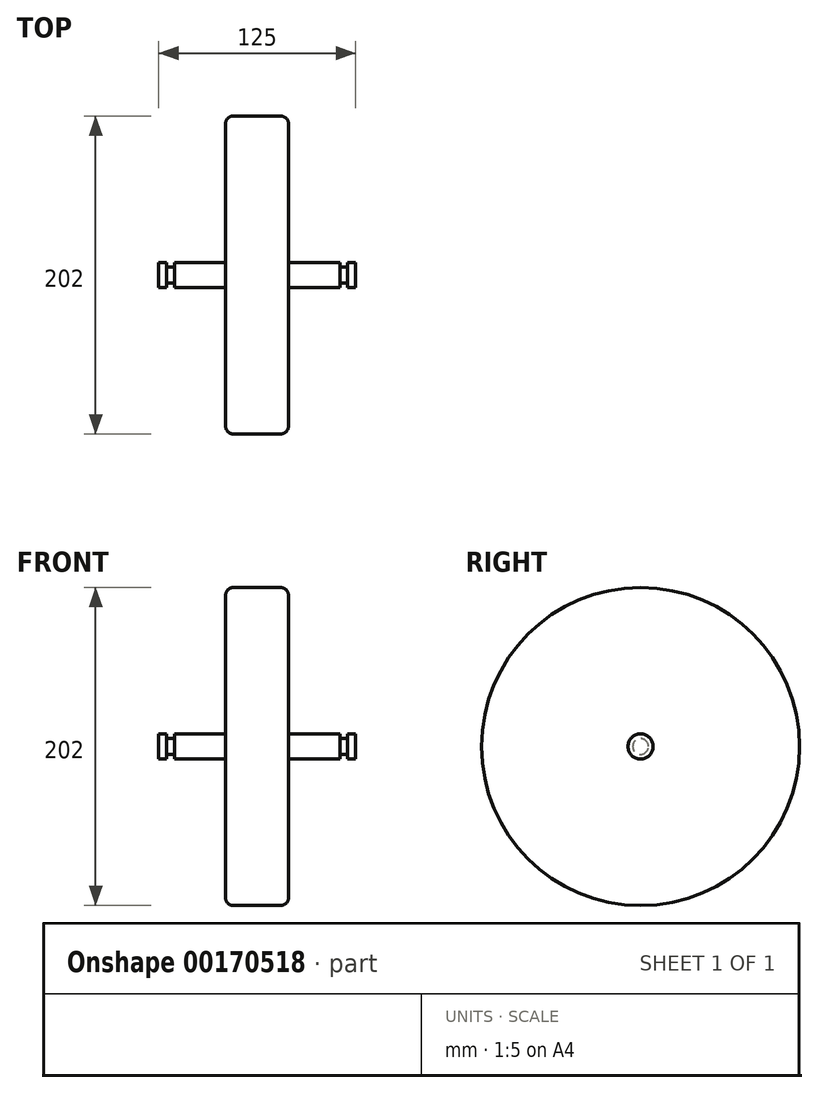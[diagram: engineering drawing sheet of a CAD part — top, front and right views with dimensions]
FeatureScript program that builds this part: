
annotation { "Feature Type Name" : "Feature", "Feature Type Description" : "" }
export const myFeature = defineFeature(function(context is Context, id is Id, definition is map)
    precondition{}
    {
        {
            var Q0;
            Q0=qCreatedBy(makeId("Front.planeOp"),FACE);
            var sketch = newSketch(context, id + "F0", { "sketchPlane" : qUnion([Q0])});
            skLineSegment(sketch, "E0", {"start": v(-87.22, 0) * mm, "end": v(73.7, 0) * mm, "construction": true});
            skLineSegment(sketch, "E1.bottom", {"start": v(-62.5, 8) * mm, "end": v(-57.5, 8) * mm});
            skLineSegment(sketch, "E1.top", {"start": v(-62.5, 0) * mm, "end": v(62.5, 0) * mm});
            skLineSegment(sketch, "E1.left", {"start": v(-62.5, 8) * mm, "end": v(-62.5, 0) * mm});
            skLineSegment(sketch, "E1.right", {"start": v(62.5, 8) * mm, "end": v(62.5, 0) * mm});
            skLineSegment(sketch, "E2.bottom", {"start": v(-15.1, 101) * mm, "end": v(14.9, 101) * mm});
            skLineSegment(sketch, "E2.top", {"start": v(-20.1, 0) * mm, "end": v(19.9, 0) * mm});
            skLineSegment(sketch, "E2.left", {"start": v(-20.1, 96) * mm, "end": v(-20.1, 8) * mm});
            skLineSegment(sketch, "E2.right", {"start": v(19.9, 96) * mm, "end": v(19.9, 8) * mm});
            skLineSegment(sketch, "E3", {"start": v(0, 0) * mm, "end": v(-0.1, 115.13) * mm, "construction": true});
            skPoint(sketch, "E3.endSnap0", {"position": v(-0.1, 101) * mm});
            skPoint(sketch, "E4.visualSharp", {"position": v(-20.1, 101) * mm});
            skArc(sketch, "E4.filletArc", {"start": v(-15.1, 101) * mm, "mid": v(-18.64, 99.54) * mm, "end": v(-20.1, 96) * mm});
            skPoint(sketch, "E5.visualSharp", {"position": v(19.9, 101) * mm});
            skArc(sketch, "E5.filletArc", {"start": v(19.9, 96) * mm, "mid": v(18.43, 99.54) * mm, "end": v(14.9, 101) * mm});
            skLineSegment(sketch, "E6.0", {"start": v(-52.5, 8) * mm, "end": v(-52.5, 5) * mm});
            skLineSegment(sketch, "E7.0", {"start": v(52.5, 8) * mm, "end": v(52.5, 5) * mm});
            skLineSegment(sketch, "E8.0", {"start": v(-57.5, 8) * mm, "end": v(-57.5, 5) * mm});
            skLineSegment(sketch, "E9.0", {"start": v(57.5, 8) * mm, "end": v(57.5, 5) * mm});
            skLineSegment(sketch, "E10.0", {"start": v(-57.5, 5) * mm, "end": v(-52.5, 5) * mm});
            skLineSegment(sketch, "E11.trimOffspring", {"start": v(52.5, 5) * mm, "end": v(57.5, 5) * mm});
            skLineSegment(sketch, "E12.trimOffspring", {"start": v(57.5, 8) * mm, "end": v(62.5, 8) * mm});
            skLineSegment(sketch, "E13.trimOffspring", {"start": v(-52.5, 8) * mm, "end": v(-20.1, 8) * mm});
            skLineSegment(sketch, "E14.trimOffspring", {"start": v(19.9, 8) * mm, "end": v(52.5, 8) * mm});
            skSolve(sketch);
        }
        {
            var Q0;
            Q0=makeQuery(id+"F0.imprint","IMPRINT",FACE,{"disambiguationData":[TD([[makeQuery(id+"F0.imprint","IMPRINT",EDGE,{"derivedFrom":sQuery(id+"F0.wireOp",EDGE,"E1.bottom")}),-1.0]])]});
            var Q1;
            Q1=sQuery(id+"F0.wireOp",EDGE,"E0");
            revolve(context, id + "F1", {"entities" : qUnion([Q0]), "axis" : qUnion([Q1]), "revolveType" : RevolveType.FULL});
        }
    });
